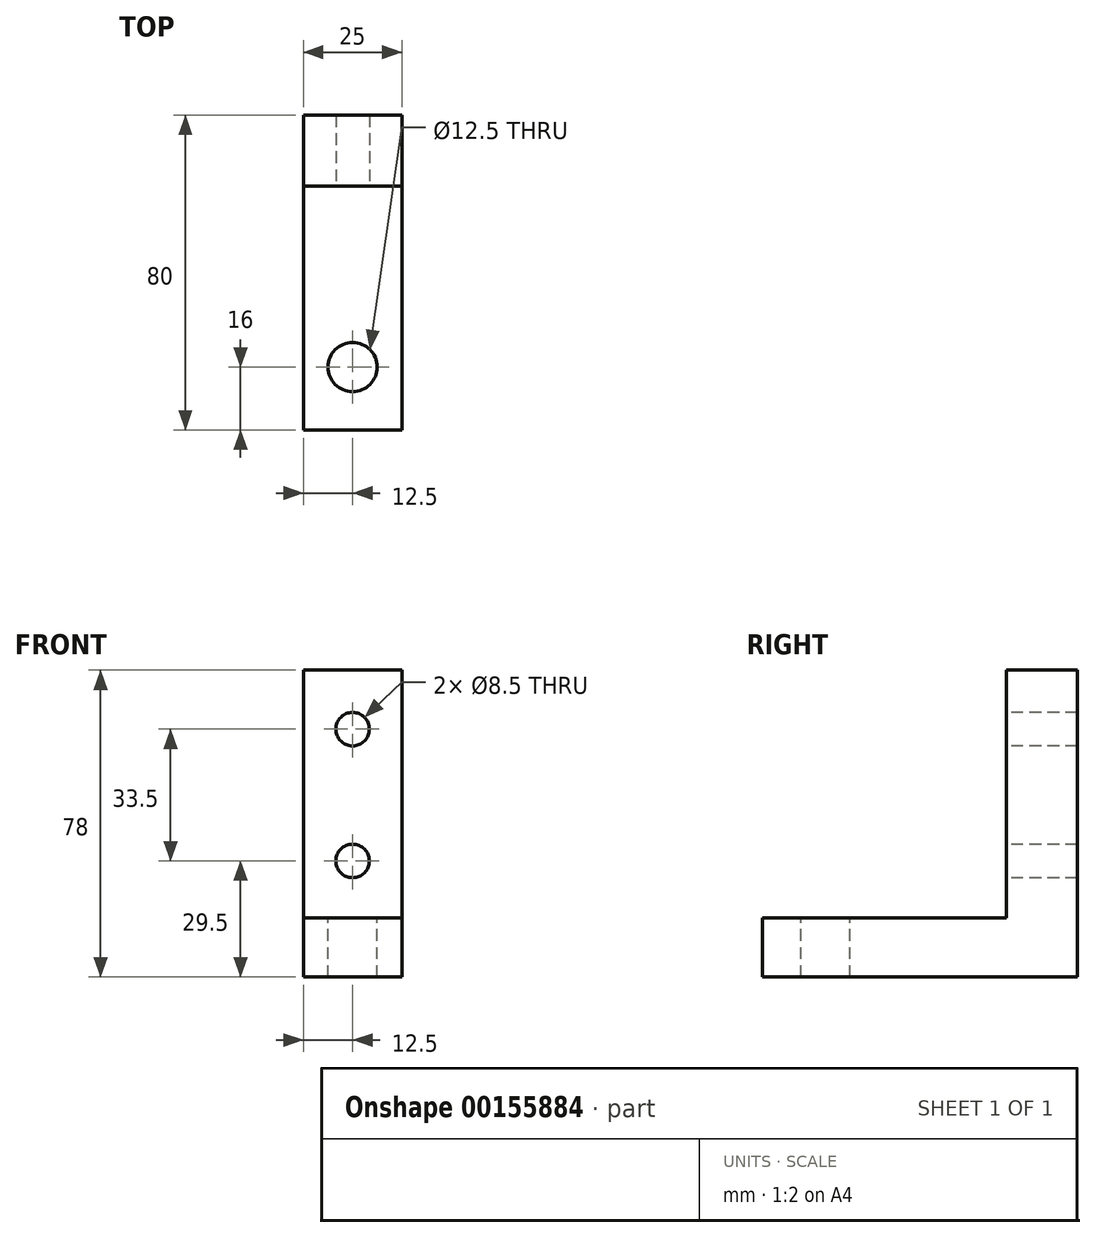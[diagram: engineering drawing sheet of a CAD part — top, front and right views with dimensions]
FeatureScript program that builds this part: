
annotation { "Feature Type Name" : "Feature", "Feature Type Description" : "" }
export const myFeature = defineFeature(function(context is Context, id is Id, definition is map)
    precondition{}
    {
        {
            var Q0;
            Q0=qCreatedBy(makeId("Front.planeOp"),FACE);
            var sketch = newSketch(context, id + "F0", { "sketchPlane" : qUnion([Q0])});
            skLineSegment(sketch, "E0.bottom", {"start": v(-12.5, 78) * mm, "end": v(12.5, 78) * mm});
            skLineSegment(sketch, "E0.top", {"start": v(-12.5, 0) * mm, "end": v(12.5, 0) * mm});
            skLineSegment(sketch, "E0.left", {"start": v(-12.5, 78) * mm, "end": v(-12.5, 0) * mm});
            skLineSegment(sketch, "E0.right", {"start": v(12.5, 78) * mm, "end": v(12.5, 0) * mm});
            skLineSegment(sketch, "E1.top", {"start": v(-12.5, 15) * mm, "end": v(12.5, 15) * mm});
            skLineSegment(sketch, "E1.left", {"start": v(-12.5, 0) * mm, "end": v(-12.5, 15) * mm});
            skLineSegment(sketch, "E1.right", {"start": v(12.5, 0) * mm, "end": v(12.5, 15) * mm});
            skCircle(sketch, "E2", {"center": v(0, 63) * mm, "radius": 4.25 * mm});
            skCircle(sketch, "E3", {"center": v(0, 29.5) * mm, "radius": 4.25 * mm});
            skSolve(sketch);
        }
        {
            var Q0;
            Q0=makeQuery(id+"F0.imprint","IMPRINT",FACE,{"disambiguationData":[TD([[makeQuery(id+"F0.imprint","IMPRINT",EDGE,{"derivedFrom":sQuery(id+"F0.wireOp",EDGE,"E0.top")}),1.0]])]});
            var Q1;
            Q1=makeQuery(id+"F0.imprint","IMPRINT",FACE,{"disambiguationData":[TD([[makeQuery(id+"F0.imprint","IMPRINT",EDGE,{"derivedFrom":sQuery(id+"F0.wireOp",EDGE,"E0.bottom")}),-1.0]])]});
            extrude(context, id + "F1", {"entities" : qUnion([Q0, Q1]), "oppositeDirection" : true, "depth" : 18 * mm});
        }
        {
            var Q0;
            Q0=makeQuery(id+"F0.imprint","IMPRINT",FACE,{"disambiguationData":[TD([[makeQuery(id+"F0.imprint","IMPRINT",EDGE,{"derivedFrom":sQuery(id+"F0.wireOp",EDGE,"E0.top")}),1.0]])]});
            extrude(context, id + "F2", {"entities" : qUnion([Q0]), "operationType" : NewBodyOperationType.ADD, "depth" : 62 * mm});
        }
        {
            var Q0;
            Q0=makeQuery(id+"F2.opExtrude","SWEPT_FACE",FACE,{"disambiguationData":[OSD([sQuery(id+"F0.wireOp",EDGE,"E1.top")])]});
            var sketch = newSketch(context, id + "F3", { "sketchPlane" : qUnion([Q0])});
            skCircle(sketch, "E4", {"center": v(0, -46) * mm, "radius": 6.25 * mm});
            skPoint(sketch, "E4.centerSnap0", {"position": v(0, -62) * mm});
            skSolve(sketch);
        }
        {
            var Q0;
            Q0=makeQuery(id+"F3.imprint","IMPRINT",FACE,{"disambiguationData":[TD([[makeQuery(id+"F3.imprint","IMPRINT",EDGE,{"derivedFrom":sQuery(id+"F3.wireOp",EDGE,"E4")}),1.0]])]});
            extrude(context, id + "F4", {"entities" : qUnion([Q0]), "operationType" : NewBodyOperationType.REMOVE, "oppositeDirection" : true, "depth" : 25.4 * mm});
        }
    });
